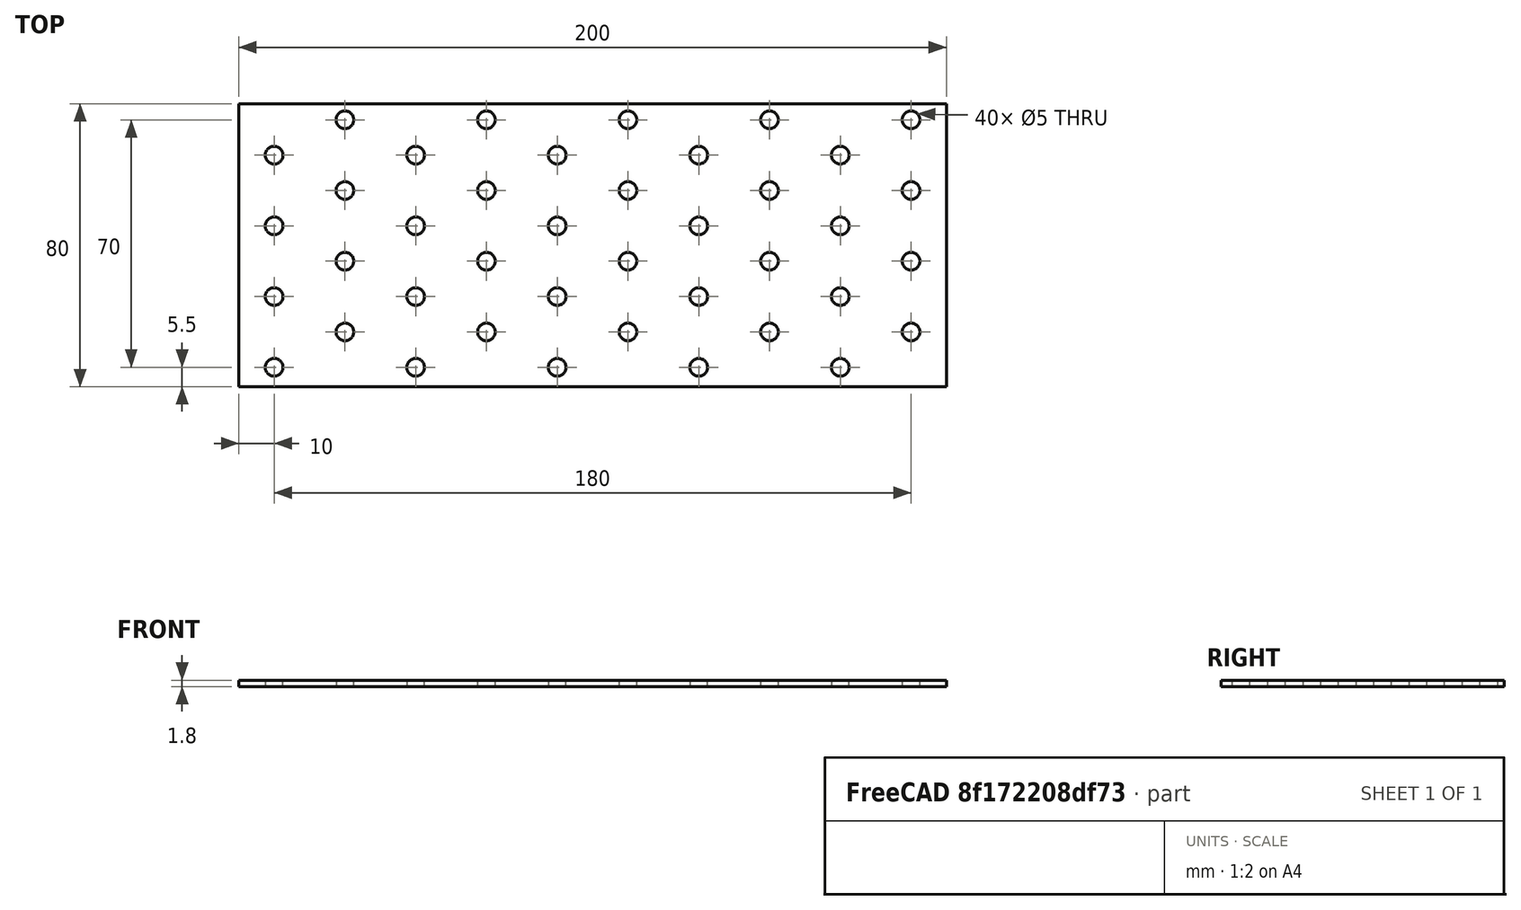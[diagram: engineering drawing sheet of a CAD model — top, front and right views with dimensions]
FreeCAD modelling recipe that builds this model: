
FCSTD DOCUMENT  (FreeCAD 0.19R24276 (Git))
Label: Bar_80x200__1_8mm_2
License: All rights reserved
LicenseURL: http://en.wikipedia.org/wiki/All_rights_reserved
objects: Sketcher::SketchObject×1, PartDesign::Pad×1, PartDesign::Body×1
note: 4 computed .brp shape members not serialized (recipe doc carries the construction recipe); baked Part::Feature solids carry a one-line shape summary decoded from their .brp

FEATURE [Sketcher::SketchObject] Sketch
  FullyConstrained = false
  MapMode = 5
  Support = -> [XY_Plane]
  sketch-geometry (44):
    g0: Circle CenterX=0 CenterY=0 CenterZ=0 NormalX=0 NormalY=0 NormalZ=1 AngleXU=0 Radius=2.5
    g1: Circle CenterX=0 CenterY=20 CenterZ=0 NormalX=0 NormalY=0 NormalZ=1 AngleXU=0 Radius=2.5
    g2: Circle CenterX=0 CenterY=40 CenterZ=0 NormalX=0 NormalY=0 NormalZ=1 AngleXU=0 Radius=2.5
    g3: Circle CenterX=0 CenterY=60 CenterZ=0 NormalX=0 NormalY=0 NormalZ=1 AngleXU=0 Radius=2.5
    g4: Circle CenterX=20 CenterY=10 CenterZ=0 NormalX=0 NormalY=0 NormalZ=1 AngleXU=0 Radius=2.5
    g5: Circle CenterX=20 CenterY=30 CenterZ=0 NormalX=0 NormalY=0 NormalZ=1 AngleXU=0 Radius=2.5
    g6: Circle CenterX=20 CenterY=50 CenterZ=0 NormalX=0 NormalY=0 NormalZ=1 AngleXU=0 Radius=2.5
    g7: Circle CenterX=20 CenterY=70 CenterZ=0 NormalX=0 NormalY=0 NormalZ=1 AngleXU=0 Radius=2.5
    g8: Circle CenterX=40 CenterY=0 CenterZ=0 NormalX=0 NormalY=0 NormalZ=1 AngleXU=0 Radius=2.5
    g9: Circle CenterX=40 CenterY=20 CenterZ=0 NormalX=0 NormalY=0 NormalZ=1 AngleXU=0 Radius=2.5
    g10: Circle CenterX=40 CenterY=40 CenterZ=0 NormalX=0 NormalY=0 NormalZ=1 AngleXU=0 Radius=2.5
    g11: Circle CenterX=40 CenterY=60 CenterZ=0 NormalX=0 NormalY=0 NormalZ=1 AngleXU=0 Radius=2.5
    g12: Circle CenterX=60 CenterY=10 CenterZ=0 NormalX=0 NormalY=0 NormalZ=1 AngleXU=0 Radius=2.5
    g13: Circle CenterX=60 CenterY=30 CenterZ=0 NormalX=0 NormalY=0 NormalZ=1 AngleXU=0 Radius=2.5
    g14: Circle CenterX=60 CenterY=50 CenterZ=0 NormalX=0 NormalY=0 NormalZ=1 AngleXU=0 Radius=2.5
    g15: Circle CenterX=60 CenterY=70 CenterZ=0 NormalX=0 NormalY=0 NormalZ=1 AngleXU=0 Radius=2.5
    g16: Circle CenterX=80 CenterY=-2e-16 CenterZ=0 NormalX=0 NormalY=0 NormalZ=1 AngleXU=0 Radius=2.5
    g17: Circle CenterX=80 CenterY=20 CenterZ=0 NormalX=0 NormalY=0 NormalZ=1 AngleXU=0 Radius=2.5
    g18: Circle CenterX=80 CenterY=40 CenterZ=0 NormalX=0 NormalY=0 NormalZ=1 AngleXU=0 Radius=2.5
    g19: Circle CenterX=80 CenterY=60 CenterZ=0 NormalX=0 NormalY=0 NormalZ=1 AngleXU=0 Radius=2.5
    g20: Circle CenterX=100 CenterY=10 CenterZ=0 NormalX=0 NormalY=0 NormalZ=1 AngleXU=0 Radius=2.5
    g21: Circle CenterX=100 CenterY=30 CenterZ=0 NormalX=0 NormalY=0 NormalZ=1 AngleXU=0 Radius=2.5
    g22: Circle CenterX=100 CenterY=50 CenterZ=0 NormalX=0 NormalY=0 NormalZ=1 AngleXU=0 Radius=2.5
    g23: Circle CenterX=100 CenterY=70 CenterZ=0 NormalX=0 NormalY=0 NormalZ=1 AngleXU=0 Radius=2.5
    g24: Circle CenterX=120 CenterY=0 CenterZ=0 NormalX=0 NormalY=0 NormalZ=1 AngleXU=0 Radius=2.5
    g25: Circle CenterX=120 CenterY=20 CenterZ=0 NormalX=0 NormalY=0 NormalZ=1 AngleXU=0 Radius=2.5
    g26: Circle CenterX=120 CenterY=40 CenterZ=0 NormalX=0 NormalY=0 NormalZ=1 AngleXU=0 Radius=2.5
    g27: Circle CenterX=120 CenterY=60 CenterZ=0 NormalX=0 NormalY=0 NormalZ=1 AngleXU=0 Radius=2.5
    g28: Circle CenterX=140 CenterY=10 CenterZ=0 NormalX=0 NormalY=0 NormalZ=1 AngleXU=0 Radius=2.5
    g29: Circle CenterX=140 CenterY=30 CenterZ=0 NormalX=0 NormalY=0 NormalZ=1 AngleXU=0 Radius=2.5
    g30: Circle CenterX=140 CenterY=50 CenterZ=0 NormalX=0 NormalY=0 NormalZ=1 AngleXU=0 Radius=2.5
    g31: Circle CenterX=140 CenterY=70 CenterZ=0 NormalX=0 NormalY=0 NormalZ=1 AngleXU=0 Radius=2.5
    g32: LineSegment StartX=-10 StartY=74.5 StartZ=0 EndX=190 EndY=74.5 EndZ=0
    g33: LineSegment StartX=190 StartY=74.5 StartZ=0 EndX=190 EndY=-5.5 EndZ=0
    g34: LineSegment StartX=190 StartY=-5.5 StartZ=0 EndX=-10 EndY=-5.5 EndZ=0
    g35: LineSegment StartX=-10 StartY=-5.5 StartZ=0 EndX=-10 EndY=74.5 EndZ=0
    g36: Circle CenterX=160 CenterY=3.6e-15 CenterZ=0 NormalX=0 NormalY=0 NormalZ=1 AngleXU=0 Radius=2.5
    g37: Circle CenterX=160 CenterY=20 CenterZ=0 NormalX=0 NormalY=0 NormalZ=1 AngleXU=0 Radius=2.5
    g38: Circle CenterX=160 CenterY=40 CenterZ=0 NormalX=0 NormalY=0 NormalZ=1 AngleXU=0 Radius=2.5
    g39: Circle CenterX=160 CenterY=60 CenterZ=0 NormalX=0 NormalY=0 NormalZ=1 AngleXU=0 Radius=2.5
    g40: Circle CenterX=180 CenterY=10 CenterZ=0 NormalX=0 NormalY=0 NormalZ=1 AngleXU=0 Radius=2.5
    g41: Circle CenterX=180 CenterY=30 CenterZ=0 NormalX=0 NormalY=0 NormalZ=1 AngleXU=0 Radius=2.5
    g42: Circle CenterX=180 CenterY=50 CenterZ=0 NormalX=0 NormalY=0 NormalZ=1 AngleXU=0 Radius=2.5
    g43: Circle CenterX=180 CenterY=70 CenterZ=0 NormalX=0 NormalY=0 NormalZ=1 AngleXU=0 Radius=2.5
  constraints (130):
    c: Coincident(g0,g-1)
    c: PointOnObject(g1,g-2)
    c: PointOnObject(g2,g-2)
    c: PointOnObject(g3,g-2)
    c: Diameter(g0) = 5
    c: Equal(g0,g1)
    c: Equal(g0,g2)
    c: Equal(g0,g3)
    c: DistanceY(g0,g1) = 20
    c: DistanceY(g1,g2) = 20
    c: DistanceY(g2,g3) = 20
    c: Equal(g0,g4) = 5
    c: Equal(g4,g5)
    c: Equal(g4,g6)
    c: Equal(g4,g7)
    c: DistanceY(g4,g5) = 20
    c: DistanceY(g5,g6) = 20
    c: DistanceY(g6,g7) = 20
    c: DistanceY(g0,g4) = 10
    c: DistanceX(g0,g4) = 20
    c: DistanceX(g5,g4) = 0
    c: DistanceX(g6,g5) = 0
    c: DistanceX(g7,g6) = 0
    c: Equal(g0,g8) = 5
    c: Equal(g8,g9)
    c: Equal(g8,g10)
    c: Equal(g8,g11)
    c: DistanceY(g8,g9) = 20
    c: DistanceY(g9,g10) = 20
    c: DistanceY(g10,g11) = 20
    c: Equal(g8,g12) = 5
    c: Equal(g12,g13)
    c: Equal(g12,g14)
    c: Equal(g12,g15)
    c: DistanceY(g12,g13) = 20
    c: DistanceY(g13,g14) = 20
    c: DistanceY(g14,g15) = 20
    c: DistanceY(g8,g12) = 10
    c: DistanceX(g8,g12) = 20
    c: DistanceX(g13,g12) = 0
    c: DistanceX(g14,g13) = 0
    c: DistanceX(g15,g14) = 0
    c: DistanceY(g8,g0) = 0
    c: DistanceX(g9,g8) = 0
    c: DistanceX(g9,g10) = 0
    c: DistanceX(g11,g10) = 0
    c: DistanceX(g4,g8) = 20
    c: Equal(g0,g16) = 5
    c: Equal(g16,g17)
    c: Equal(g16,g18)
    c: Equal(g16,g19)
    c: DistanceY(g16,g17) = 20
    c: DistanceY(g17,g18) = 20
    c: DistanceY(g18,g19) = 20
    c: Equal(g16,g20) = 5
    c: Equal(g20,g21)
    c: Equal(g20,g22)
    c: Equal(g20,g23)
    c: DistanceY(g20,g21) = 20
    c: DistanceY(g21,g22) = 20
    c: DistanceY(g22,g23) = 20
    c: DistanceY(g16,g20) = 10
    c: DistanceX(g16,g20) = 20
    c: DistanceX(g21,g20) = 0
    c: DistanceX(g22,g21) = 0
    c: DistanceX(g23,g22) = 0
    c: Equal(g16,g24) = 5
    c: Equal(g24,g25)
    c: Equal(g24,g26)
    c: Equal(g24,g27)
    c: DistanceY(g24,g25) = 20
    c: DistanceY(g25,g26) = 20
    c: DistanceY(g26,g27) = 20
    c: Equal(g24,g28) = 5
    c: Equal(g28,g29)
    c: Equal(g28,g30)
    c: Equal(g28,g31)
    c: DistanceY(g28,g29) = 20
    c: DistanceY(g29,g30) = 20
    c: DistanceY(g30,g31) = 20
    c: DistanceY(g24,g28) = 10
    c: DistanceX(g24,g28) = 20
    c: DistanceX(g29,g28) = 0
    c: DistanceX(g30,g29) = 0
    c: DistanceX(g31,g30) = 0
    c: DistanceY(g24,g16) = 0
    c: DistanceX(g25,g24) = 0
    c: DistanceX(g25,g26) = 0
    c: DistanceX(g27,g26) = 0
    c: DistanceX(g20,g24) = 20
    c: DistanceX(g16,g17) = 0
    c: DistanceX(g17,g18) = 0
    c: DistanceX(g18,g19) = 0
    c: DistanceX(g12,g16) = 20
    c: DistanceY(g8,g16) = 0
    c: Coincident(g32,g33)
    c: Coincident(g33,g34)
    c: Coincident(g34,g35)
    c: Coincident(g35,g32)
    c: Horizontal(g32)
    c: Horizontal(g34)
    c: Vertical(g33)
    c: Vertical(g35)
    c: DistanceY(g33,g33) = 80
    c: DistanceX(g32,g32) = 200
    c: DistanceY(g34,g0) = 5.5
    c: DistanceX(g34,g0) = 10
    c: Equal(g36,g37)
    c: Equal(g36,g38)
    c: Equal(g36,g39)
    c: DistanceY(g36,g37) = 20
    c: DistanceY(g37,g38) = 20
    c: DistanceY(g38,g39) = 20
    c: Equal(g36,g40) = 5
    c: Equal(g40,g41)
    c: Equal(g40,g42)
    c: Equal(g40,g43)
    c: DistanceY(g40,g41) = 20
    c: DistanceY(g41,g42) = 20
    c: DistanceY(g42,g43) = 20
    c: DistanceY(g36,g40) = 10
    c: DistanceX(g36,g40) = 20
    c: DistanceX(g41,g40) = 0
    c: DistanceX(g42,g41) = 0
    c: DistanceX(g43,g42) = 0
    c: DistanceX(g37,g36) = 0
    c: DistanceX(g37,g38) = 0
    c: DistanceX(g39,g38) = 0
    c: DistanceY(g36,g24) = 0
    c: DistanceX(g28,g36) = 20
FEATURE [PartDesign::Pad] Pad
  Direction = (1,1,1)
  Length = 1.8
  Length2 = 100
  Profile = -> Sketch
  Type = 0
FEATURE [PartDesign::Body] Body
  Group = -> [Sketch,Pad]
  Origin = -> Origin
  Tip = -> Pad
